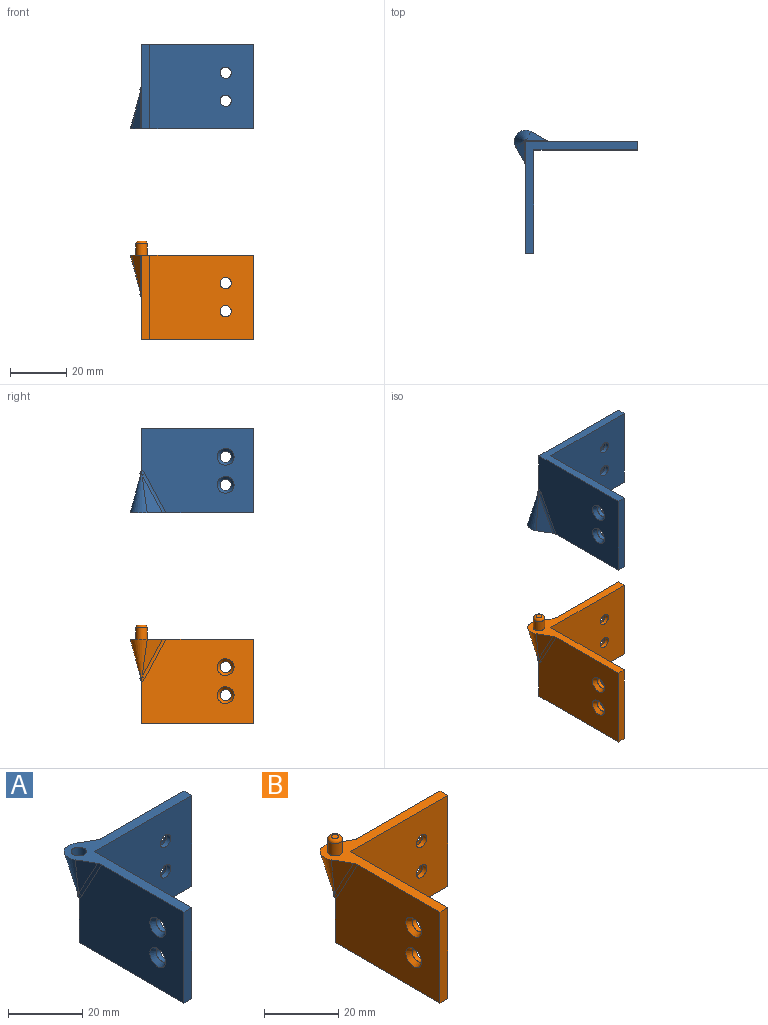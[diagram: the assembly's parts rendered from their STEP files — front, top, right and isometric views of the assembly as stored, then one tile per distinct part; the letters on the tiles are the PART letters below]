
ASSEMBLY  parts=2 mates=1
PART A: 26 faces, bbox 44x44x30.5 mm
  f0: plane 40x30mm, normal (0,1,0), area 1073.6mm2, adj f1,f5,f6,f7,f16,f17,f24,f25
  f1: plane 40x30mm, normal (-1,0,0), area 1073.6mm2, adj f0,f2,f6,f7,f14,f15,f22,f23
  f2: plane 30x3mm, normal (0,-1,0), area 90mm2, adj f1,f3,f6,f7
  f3: plane 37x30mm, normal (1,0,0), area 1084.9mm2, adj f2,f4,f6,f7,f20,f21
  f4: plane 37x30mm, normal (0,-1,0), area 1084.9mm2, adj f3,f5,f6,f7,f18,f19
  f5: plane 30x3mm, normal (1,0,0), area 90mm2, adj f0,f4,f6,f7
  f6: plane 44.03x44.03mm, normal (0,0,1), area 266.5mm2, adj f0,f1,f2,f3,f4,f5,f8,f9
  f7: plane 40x40mm, normal (0,0,-1), area 231mm2, adj f0,f1,f2,f3,f4,f5
  f8: plane 13.52x7.25mm, normal (0.48,0.84,-0.26), area 43.9mm2, adj f6,f9,f16
  f9: cone r=4mm half-angle=15deg, axis (0,0,1), area 80.4mm2, adj f6,f8,f10,f15,f17
  f10: plane 13.52x7.25mm, normal (-0.84,-0.48,-0.26), area 43.9mm2, adj f6,f9,f14
  f11: cylinder r=2.05mm len=4.1mm, axis (0,0,1), area 52.8mm2, adj f6,f13
  f12: plane 2.1x2.1mm, normal (0,0,1), area 3.5mm2, adj f13
  f13: torus R=1.05mm, axis (0,0,1), area 16.6mm2, adj f11,f12
  f14: cylinder r=2mm len=14.55mm, axis (0,-0.47,0.88), area 18.1mm2, adj f1,f6,f10,f15
  f15: bspline ~4.09x3.41mm, area 2.7mm2, adj f1,f9,f14,f17
  f16: cylinder r=2mm len=14.55mm, axis (-0.47,0,-0.88), area 18.1mm2, adj f0,f6,f8,f17
  f17: bspline ~3.86x3.52mm, area 2.7mm2, adj f0,f9,f15,f16
  f18: cylinder r=2mm len=4mm, axis (0,1,0), area 18.8mm2, adj f4,f24
  f19: cylinder r=2mm len=4mm, axis (0,1,0), area 18.8mm2, adj f4,f25
  f20: cylinder r=2mm len=4mm, axis (-1,0,0), area 18.8mm2, adj f3,f22
  f21: cylinder r=2mm len=4mm, axis (-1,0,0), area 18.8mm2, adj f3,f23
  f22: cone r=2mm half-angle=33.7deg, axis (-1,0,0), area 28.3mm2, adj f1,f20
  f23: cone r=2mm half-angle=33.7deg, axis (-1,0,0), area 28.3mm2, adj f1,f21
  f24: cone r=2mm half-angle=33.7deg, axis (0,1,0), area 28.3mm2, adj f0,f18
  f25: cone r=2mm half-angle=33.7deg, axis (0,1,0), area 28.3mm2, adj f0,f19
PART B: 26 faces, bbox 44x44x35 mm
  f0: plane 40x30mm, normal (0,1,0), area 1073.6mm2, adj f1,f5,f6,f7,f16,f17,f24,f25
  f1: plane 40x30mm, normal (-1,0,0), area 1073.6mm2, adj f0,f2,f6,f7,f14,f15,f22,f23
  f2: plane 30x3mm, normal (0,-1,0), area 90mm2, adj f1,f3,f6,f7
  f3: plane 37x30mm, normal (1,0,0), area 1084.9mm2, adj f2,f4,f6,f7,f20,f21
  f4: plane 37x30mm, normal (0,-1,0), area 1084.9mm2, adj f3,f5,f6,f7,f18,f19
  f5: plane 30x3mm, normal (1,0,0), area 90mm2, adj f0,f4,f6,f7
  f6: plane 44.03x44.03mm, normal (0,0,1), area 267.2mm2, adj f0,f1,f2,f3,f4,f5,f8,f9
  f7: plane 40x40mm, normal (0,0,-1), area 231mm2, adj f0,f1,f2,f3,f4,f5
  f8: plane 13.52x7.25mm, normal (0.48,0.84,-0.26), area 43.9mm2, adj f6,f9,f16
  f9: cone r=4mm half-angle=15deg, axis (0,0,1), area 80.4mm2, adj f6,f8,f10,f15,f17
  f10: plane 13.52x7.25mm, normal (-0.84,-0.48,-0.26), area 43.9mm2, adj f6,f9,f14
  f11: cylinder r=2mm len=4mm, axis (0,0,-1), area 50.3mm2, adj f6,f13
  f12: plane 2x2mm, normal (0,0,1), area 3.1mm2, adj f13
  f13: torus R=1mm, axis (0,0,1), area 16.2mm2, adj f11,f12
  f14: cylinder r=2mm len=14.55mm, axis (0,-0.47,0.88), area 18.1mm2, adj f1,f6,f10,f15
  f15: bspline ~4.09x3.41mm, area 2.7mm2, adj f1,f9,f14,f17
  f16: cylinder r=2mm len=14.55mm, axis (-0.47,0,-0.88), area 18.1mm2, adj f0,f6,f8,f17
  f17: bspline ~3.86x3.52mm, area 2.7mm2, adj f0,f9,f15,f16
  f18: cylinder r=2mm len=4mm, axis (0,1,0), area 18.8mm2, adj f4,f24
  f19: cylinder r=2mm len=4mm, axis (0,1,0), area 18.8mm2, adj f4,f25
  f20: cylinder r=2mm len=4mm, axis (-1,0,0), area 18.8mm2, adj f3,f22
  f21: cylinder r=2mm len=4mm, axis (-1,0,0), area 18.8mm2, adj f3,f23
  f22: cone r=2mm half-angle=33.7deg, axis (-1,0,0), area 28.3mm2, adj f1,f20
  f23: cone r=2mm half-angle=33.7deg, axis (-1,0,0), area 28.3mm2, adj f1,f21
  f24: cone r=2mm half-angle=33.7deg, axis (0,1,0), area 28.3mm2, adj f0,f18
  f25: cone r=2mm half-angle=33.7deg, axis (0,1,0), area 28.3mm2, adj f0,f19
PLACE A rot(axis=(-0.71,0.71,0),180deg) t=(0,0,105.05)mm
PLACE B at identity fixed
MATE slider A.f9 <-> B.f9  axis (0,0,-1) through (-20,20,75.05)mm
